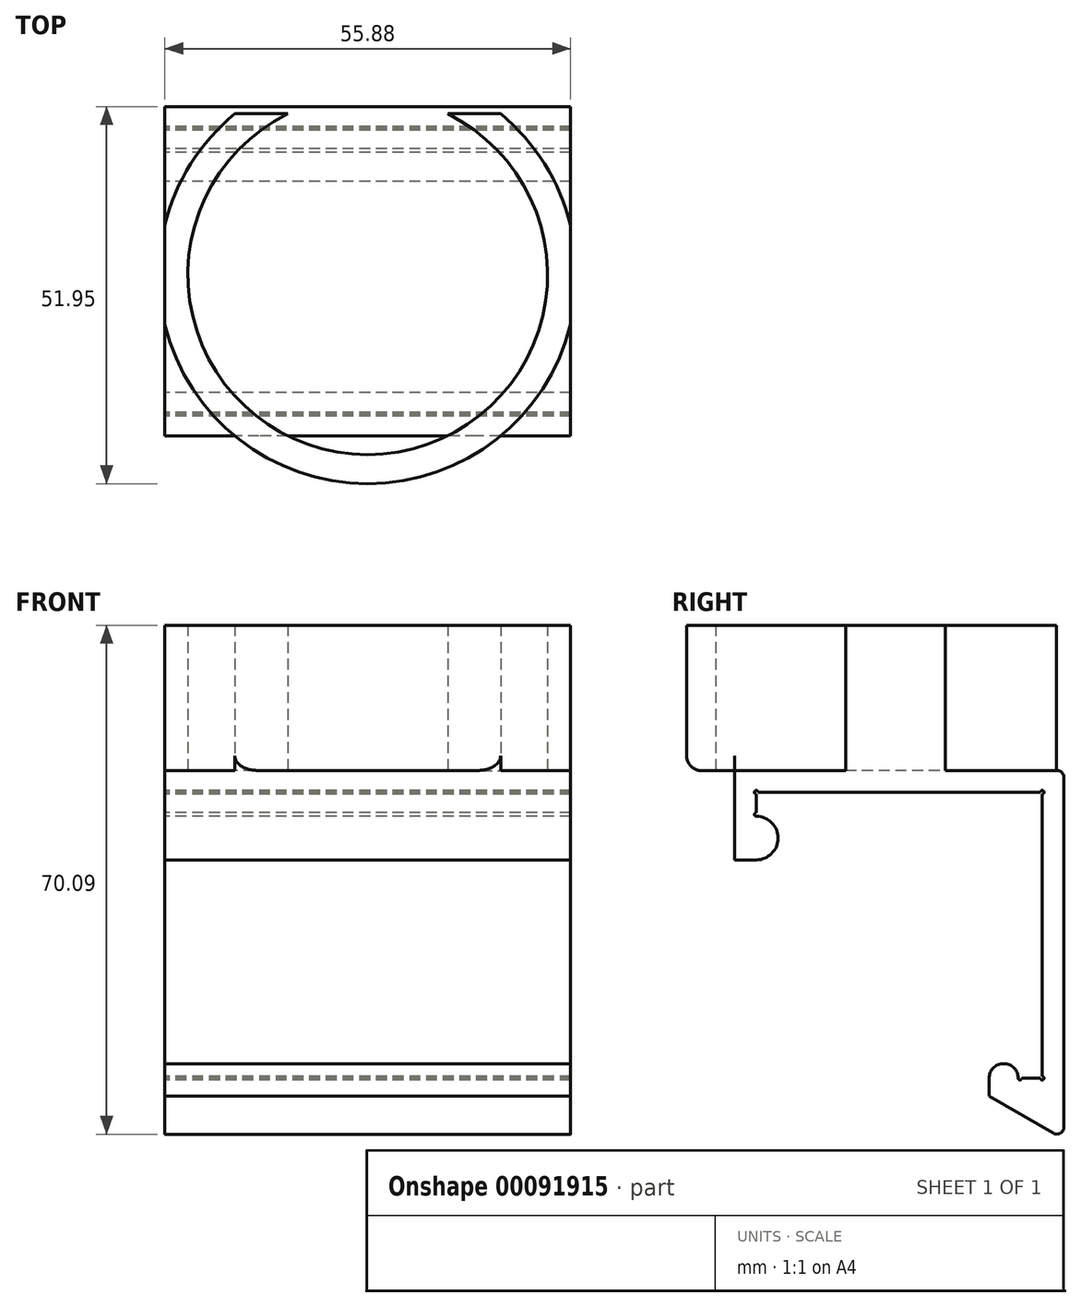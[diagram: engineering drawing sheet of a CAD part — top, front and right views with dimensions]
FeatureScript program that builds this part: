
annotation { "Feature Type Name" : "Feature", "Feature Type Description" : "" }
export const myFeature = defineFeature(function(context is Context, id is Id, definition is map)
    precondition{}
    {
        {
            var Q0;
            Q0=qCreatedBy(makeId("Right.planeOp"),FACE);
            var sketch = newSketch(context, id + "F0", { "sketchPlane" : qUnion([Q0])});
            skLineSegment(sketch, "E0", {"start": v(-45.37, 0) * mm, "end": v(0, 0) * mm});
            skLineSegment(sketch, "E1", {"start": v(0, 0) * mm, "end": v(0, -50.82) * mm});
            skLineSegment(sketch, "E2", {"start": v(-3, -42.12) * mm, "end": v(-3, -3.25) * mm});
            skLineSegment(sketch, "E3", {"start": v(-3.25, -3) * mm, "end": v(-42.12, -3) * mm});
            skLineSegment(sketch, "E4", {"start": v(-45.37, 0) * mm, "end": v(-45.37, -12.3) * mm});
            skLineSegment(sketch, "E5", {"start": v(-45.37, -12.3) * mm, "end": v(-42.37, -12.3) * mm});
            skArc(sketch, "E6", {"start": v(-42.37, -12.3) * mm, "mid": v(-39.37, -9.3) * mm, "end": v(-42.37, -6.3) * mm});
            skLineSegment(sketch, "E7", {"start": v(0, -50.82) * mm, "end": v(-10.86, -50.82) * mm, "construction": true});
            skLineSegment(sketch, "E8", {"start": v(-10.3, -42.37) * mm, "end": v(-10.3, -44.87) * mm});
            skLineSegment(sketch, "E9", {"start": v(-10.3, -44.87) * mm, "end": v(0, -50.82) * mm});
            skArc(sketch, "E10", {"start": v(-10.3, -42.37) * mm, "mid": v(-8.3, -40.37) * mm, "end": v(-6.3, -42.37) * mm});
            skArc(sketch, "E11", {"start": v(-42.37, -6.3) * mm, "mid": v(-42.62, -6.05) * mm, "end": v(-42.37, -5.8) * mm});
            skLineSegment(sketch, "E12", {"start": v(-42.37, -3.25) * mm, "end": v(-42.37, -5.8) * mm});
            skArc(sketch, "E13", {"start": v(-3.25, -42.37) * mm, "mid": v(-2.82, -42.55) * mm, "end": v(-3, -42.12) * mm});
            skArc(sketch, "E14", {"start": v(-6.3, -42.37) * mm, "mid": v(-6.05, -42.62) * mm, "end": v(-5.8, -42.37) * mm});
            skLineSegment(sketch, "E15.trimOffspring", {"start": v(-5.8, -42.37) * mm, "end": v(-3.25, -42.37) * mm});
            skArc(sketch, "E16", {"start": v(-3, -3.25) * mm, "mid": v(-2.82, -2.82) * mm, "end": v(-3.25, -3) * mm});
            skArc(sketch, "E17", {"start": v(-42.12, -3) * mm, "mid": v(-42.55, -2.82) * mm, "end": v(-42.37, -3.25) * mm});
            skSolve(sketch);
        }
        {
            var Q0;
            Q0=makeQuery(id+"F0.imprint","IMPRINT",FACE,{"disambiguationData":[TD([[makeQuery(id+"F0.imprint","IMPRINT",EDGE,{"derivedFrom":sQuery(id+"F0.wireOp",EDGE,"E0")}),-1.0]])]});
            extrude(context, id + "F1", {"entities" : qUnion([Q0]), "depth" : 55.88 * mm});
        }
        {
            var Q0;
            Q0=makeQuery(id+"F1.opExtrude","SWEPT_EDGE",EDGE,{"disambiguationData":[OSD([sQuery(id+"F0.wireOp",EDGE,"E1"),sQuery(id+"F0.wireOp",EDGE,"8Mj782aS-toYm-4woD-4NwG-GUfMlXjbYWet")])]});
            fillet(context, id + "F2", {"entities" : qUnion([Q0]), "radius" : 1 * mm, "tangentPropagation" : true, "allowEdgeOverflow" : false});
        }
        {
            var Q0;
            Q0=makeQuery(id+"F1.opExtrude","SWEPT_FACE",FACE,{"disambiguationData":[OSD([sQuery(id+"F0.wireOp",EDGE,"E0")])]});
            var sketch = newSketch(context, id + "F3", { "sketchPlane" : qUnion([Q0])});
            skCircle(sketch, "E18", {"center": v(27.94, -23.19) * mm, "radius": 24.77 * mm});
            skPoint(sketch, "E18.centerSnap0", {"position": v(27.94, -45.37) * mm});
            skPoint(sketch, "E18.centerSnap1", {"position": v(0, -23.19) * mm});
            skCircle(sketch, "E19", {"center": v(27.94, -23.19) * mm, "radius": 28.77 * mm});
            skSolve(sketch);
        }
        {
            var Q0;
            {var subQ0=sQuery(id+"F3.wireOp",EDGE,"E18");var subQ1=sQuery(id+"F0.wireOp",EDGE,"E0");var subQ4=makeQuery(id+"F1.opExtrude","SWEPT_EDGE",EDGE,{"disambiguationData":[OSD([subQ1,sQuery(id+"F0.wireOp",EDGE,"E4")])]});var subQ5=makeQuery(id+"F3.imprint","INTERSECT",VERTEX,{"disambiguationData":[OD(1.0)],"derivedFrom":[subQ4,subQ0]});Q0=makeQuery(id+"F3.imprint","IMPRINT",FACE,{"disambiguationData":[TD([[makeQuery(id+"F3.imprint","IMPRINT",EDGE,{"disambiguationData":[TD([[subQ5,-1.0]])],"derivedFrom":subQ0}),-1.0]])]});}
            var Q1;
            {var subQ0=sQuery(id+"F3.wireOp",EDGE,"E18");var subQ1=sQuery(id+"F0.wireOp",EDGE,"E0");var subQ4=makeQuery(id+"F1.opExtrude","SWEPT_EDGE",EDGE,{"disambiguationData":[OSD([subQ1,sQuery(id+"F0.wireOp",EDGE,"E4")])]});var subQ5=makeQuery(id+"F3.imprint","INTERSECT",VERTEX,{"disambiguationData":[OD(0.0)],"derivedFrom":[subQ4,subQ0]});Q1=makeQuery(id+"F3.imprint","IMPRINT",FACE,{"disambiguationData":[TD([[makeQuery(id+"F3.imprint","IMPRINT",EDGE,{"disambiguationData":[TD([[subQ5,1.0]])],"derivedFrom":subQ0}),-1.0]])]});}
            var Q2;
            {var subQ1=sQuery(id+"F0.wireOp",EDGE,"E0");var subQ4=makeQuery(id+"F1.opExtrude","CAP_EDGE",EDGE,{"disambiguationData":[OSD([subQ1])],"isStart":true});var subQ6=sQuery(id+"F3.wireOp",EDGE,"E19");var subQ8=makeQuery(id+"F3.imprint","INTERSECT",VERTEX,{"disambiguationData":[OD(0.0)],"derivedFrom":[subQ4,subQ6]});Q2=makeQuery(id+"F3.imprint","IMPRINT",FACE,{"disambiguationData":[TD([[makeQuery(id+"F3.imprint","IMPRINT",EDGE,{"disambiguationData":[TD([[subQ8,1.0]])],"derivedFrom":subQ4}),-1.0]])]});}
            var Q3;
            {var subQ1=sQuery(id+"F0.wireOp",EDGE,"E0");var subQ4=makeQuery(id+"F1.opExtrude","CAP_EDGE",EDGE,{"disambiguationData":[OSD([subQ1])],"isStart":false});var subQ6=sQuery(id+"F3.wireOp",EDGE,"E19");var subQ8=makeQuery(id+"F3.imprint","INTERSECT",VERTEX,{"disambiguationData":[OD(0.0)],"derivedFrom":[subQ4,subQ6]});Q3=makeQuery(id+"F3.imprint","IMPRINT",FACE,{"disambiguationData":[TD([[makeQuery(id+"F3.imprint","IMPRINT",EDGE,{"disambiguationData":[TD([[subQ8,1.0]])],"derivedFrom":subQ4}),1.0]])]});}
            extrude(context, id + "F4", {"entities" : qUnion([Q0, Q1, Q2, Q3]), "operationType" : NewBodyOperationType.ADD, "depth" : 20 * mm});
        }
        {
            var Q0;
            Q0=makeQuery(id+"F4.opExtrude","CAP_EDGE",EDGE,{"disambiguationData":[OSD([sQuery(id+"F3.wireOp",EDGE,"E19")])],"isStart":true});
            fillet(context, id + "F5", {"entities" : qUnion([Q0]), "radius" : 2 * mm, "tangentPropagation" : true, "allowEdgeOverflow" : false});
        }
    });
